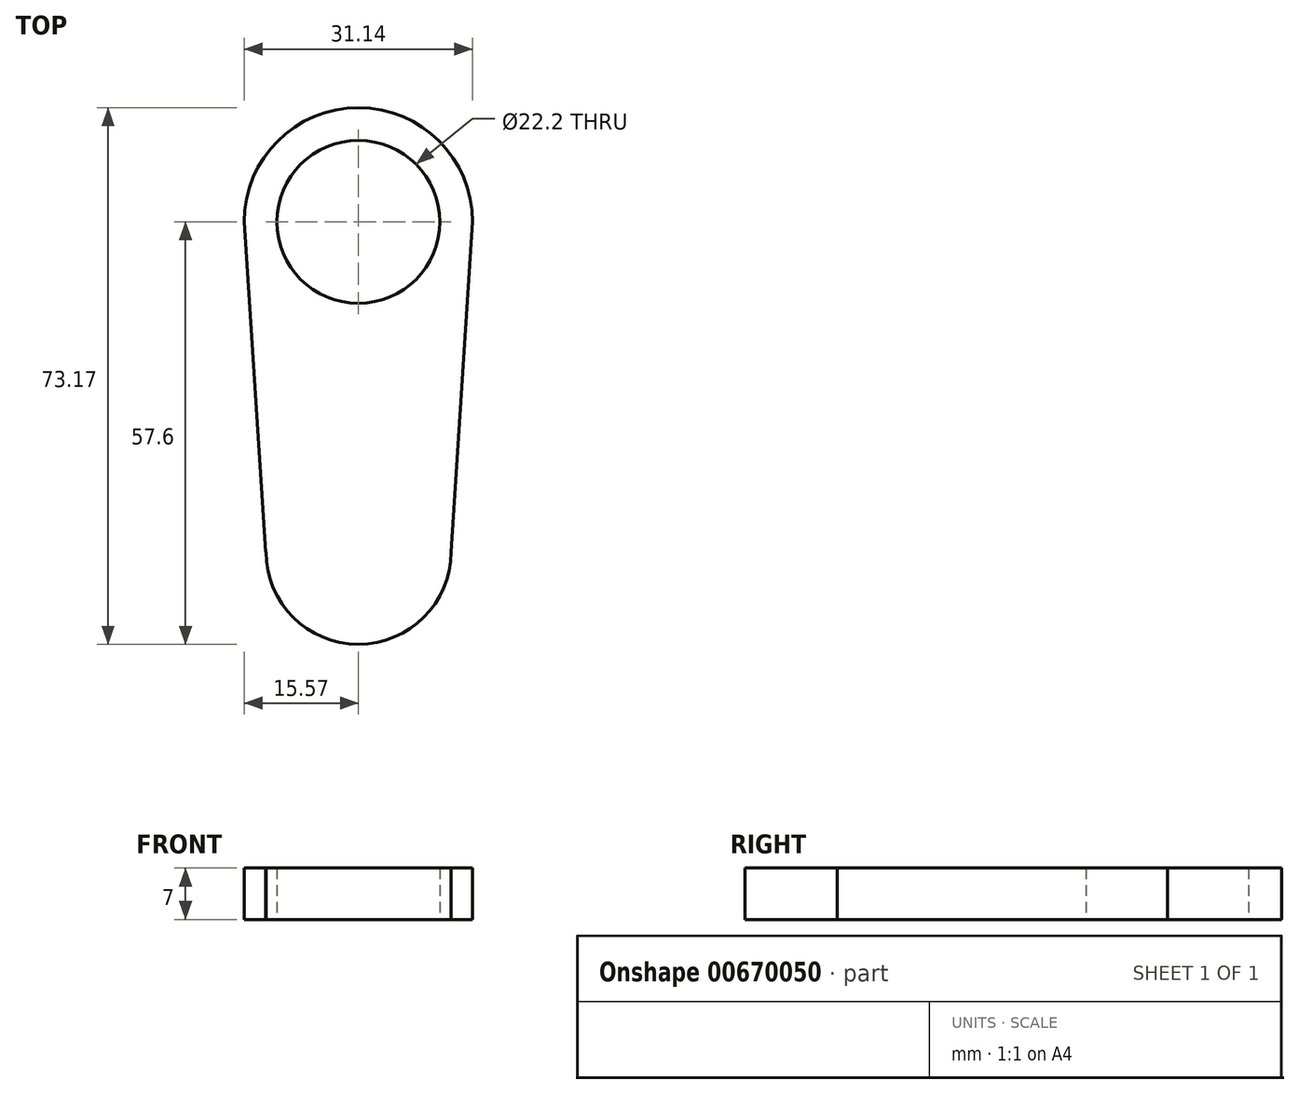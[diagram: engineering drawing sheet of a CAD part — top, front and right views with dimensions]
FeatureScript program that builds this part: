
annotation { "Feature Type Name" : "Feature", "Feature Type Description" : "" }
export const myFeature = defineFeature(function(context is Context, id is Id, definition is map)
    precondition{}
    {
        {
            var Q0;
            Q0=qCreatedBy(makeId("Top.planeOp"),FACE);
            var sketch = newSketch(context, id + "F0", { "sketchPlane" : qUnion([Q0])});
            skCircle(sketch, "E0", {"center": v(0, 0) * mm, "radius": 12.6 * mm});
            skLineSegment(sketch, "E1", {"start": v(0, 0) * mm, "end": v(0, 45) * mm});
            skCircle(sketch, "E2", {"center": v(0, 45) * mm, "radius": 11.1 * mm});
            skArc(sketch, "E3", {"start": v(0, 60.57) * mm, "mid": v(11.01, 56.01) * mm, "end": v(15.57, 45) * mm});
            skArc(sketch, "E4", {"start": v(0, 60.57) * mm, "mid": v(-11.01, 56.01) * mm, "end": v(-15.57, 45) * mm});
            skLineSegment(sketch, "E5", {"start": v(-15.57, 45) * mm, "end": v(-12.63, 0) * mm});
            skLineSegment(sketch, "E6", {"start": v(-12.63, 0) * mm, "end": v(12.6, 0) * mm});
            skLineSegment(sketch, "E7", {"start": v(12.6, 0) * mm, "end": v(15.57, 45) * mm});
            skSolve(sketch);
        }
        {
            var Q0;
            Q0 = qSketchRegion(id + "F0", true);
            extrude(context, id + "F1", {"entities" : qUnion([Q0]), "depth" : 7 * mm, "offsetDistance" : 25.4 * mm});
        }
    });
